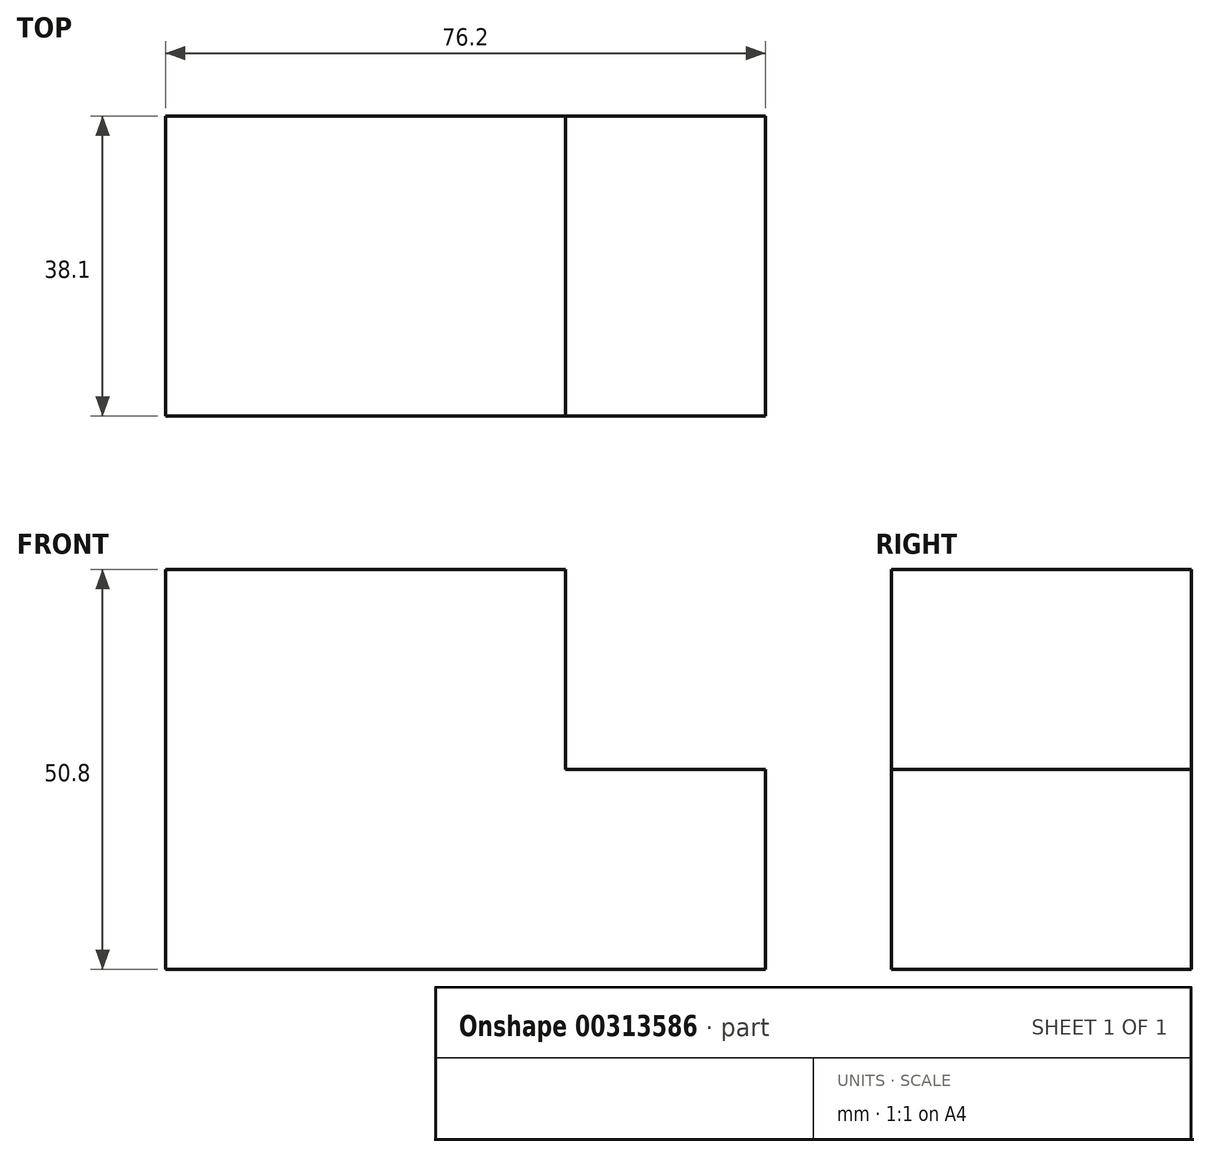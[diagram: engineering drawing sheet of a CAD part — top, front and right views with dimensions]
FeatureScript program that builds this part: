
annotation { "Feature Type Name" : "Feature", "Feature Type Description" : "" }
export const myFeature = defineFeature(function(context is Context, id is Id, definition is map)
    precondition{}
    {
        {
            var Q0;
            Q0=qCreatedBy(makeId("Front.planeOp"),FACE);
            var sketch = newSketch(context, id + "F0", { "sketchPlane" : qUnion([Q0])});
            skLineSegment(sketch, "E0", {"start": v(-32.57, -54.6) * mm, "end": v(43.63, -54.6) * mm});
            skLineSegment(sketch, "E1", {"start": v(43.63, -54.6) * mm, "end": v(43.63, -29.2) * mm});
            skLineSegment(sketch, "E2", {"start": v(43.63, -29.2) * mm, "end": v(18.23, -29.2) * mm});
            skLineSegment(sketch, "E3", {"start": v(18.23, -29.2) * mm, "end": v(18.23, -3.8) * mm});
            skLineSegment(sketch, "E4", {"start": v(18.23, -3.8) * mm, "end": v(-32.57, -3.8) * mm});
            skLineSegment(sketch, "E5", {"start": v(-32.57, -3.8) * mm, "end": v(-32.57, -54.6) * mm});
            skSolve(sketch);
        }
        {
            var Q0;
            Q0=makeQuery(id+"F0.imprint","IMPRINT",FACE,{"disambiguationData":[TD([[makeQuery(id+"F0.imprint","IMPRINT",EDGE,{"derivedFrom":sQuery(id+"F0.wireOp",EDGE,"E0")}),1.0]])]});
            extrude(context, id + "F1", {"entities" : qUnion([Q0]), "oppositeDirection" : true, "depth" : 38.1 * mm});
        }
    });
